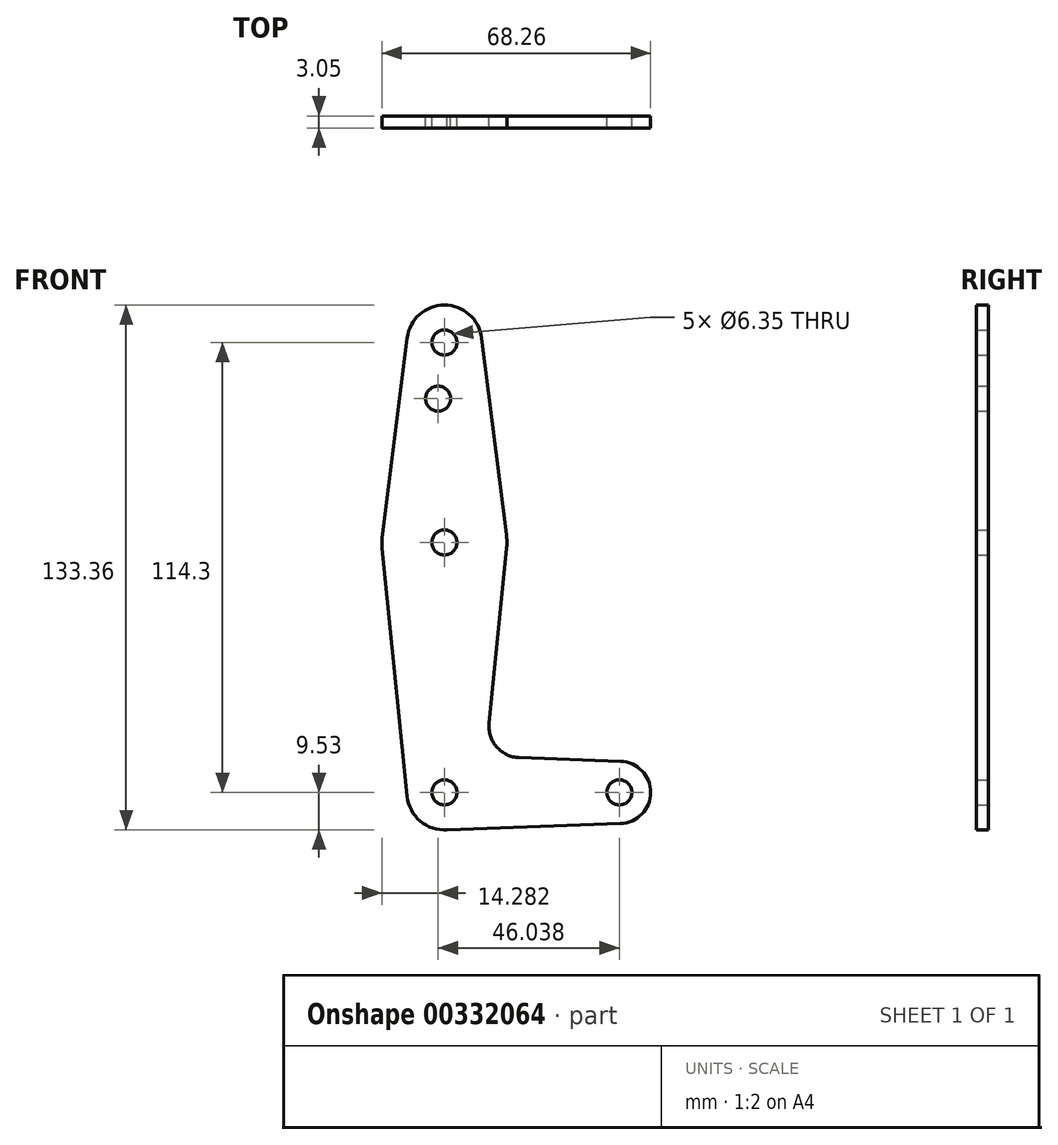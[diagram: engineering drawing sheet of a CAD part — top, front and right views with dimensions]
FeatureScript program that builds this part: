
annotation { "Feature Type Name" : "Feature", "Feature Type Description" : "" }
export const myFeature = defineFeature(function(context is Context, id is Id, definition is map)
    precondition{}
    {
        {
            var Q0;
            Q0=qCreatedBy(makeId("Front.planeOp"),FACE);
            var sketch = newSketch(context, id + "F0", { "sketchPlane" : qUnion([Q0])});
            skLineSegment(sketch, "E0", {"start": v(0, 0) * mm, "end": v(0, 114.3) * mm, "construction": true});
            skLineSegment(sketch, "E1", {"start": v(0, 0) * mm, "end": v(44.45, 0) * mm, "construction": true});
            skCircle(sketch, "E2", {"center": v(0, 114.3) * mm, "radius": 9.53 * mm});
            skCircle(sketch, "E3", {"center": v(0, 63.5) * mm, "radius": 15.88 * mm});
            skCircle(sketch, "E4", {"center": v(0, 0) * mm, "radius": 9.53 * mm});
            skCircle(sketch, "E5", {"center": v(44.45, 0) * mm, "radius": 7.94 * mm});
            skLineSegment(sketch, "E6", {"start": v(9.45, 115.5) * mm, "end": v(16, 63.46) * mm});
            skLineSegment(sketch, "E7", {"start": v(15.8, 61.91) * mm, "end": v(11.34, 17.59) * mm});
            skLineSegment(sketch, "E8", {"start": v(18.97, 8.85) * mm, "end": v(44.73, 7.93) * mm});
            skLineSegment(sketch, "E9", {"start": v(0, -9.52) * mm, "end": v(44.73, -7.93) * mm});
            skLineSegment(sketch, "E10", {"start": v(-15.8, 61.91) * mm, "end": v(-9.48, -0.95) * mm});
            skLineSegment(sketch, "E11", {"start": v(-9.45, 115.5) * mm, "end": v(-15.75, 65.48) * mm});
            skCircle(sketch, "E12", {"center": v(0, 114.3) * mm, "radius": 3.18 * mm});
            skCircle(sketch, "E13", {"center": v(0, 0) * mm, "radius": 3.18 * mm});
            skCircle(sketch, "E14", {"center": v(0, 63.5) * mm, "radius": 3.18 * mm});
            skCircle(sketch, "E15", {"center": v(44.45, 0) * mm, "radius": 3.18 * mm});
            skArc(sketch, "E16.filletArc", {"start": v(11.34, 17.59) * mm, "mid": v(13.26, 11.57) * mm, "end": v(18.97, 8.85) * mm});
            skCircle(sketch, "E17", {"center": v(-1.59, 100.03) * mm, "radius": 3.18 * mm});
            skSolve(sketch);
        }
        {
            var Q0;
            Q0 = qSketchRegion(id + "F0", true);
            extrude(context, id + "F1", {"entities" : qUnion([Q0]), "depth" : 3.05 * mm});
        }
    });
